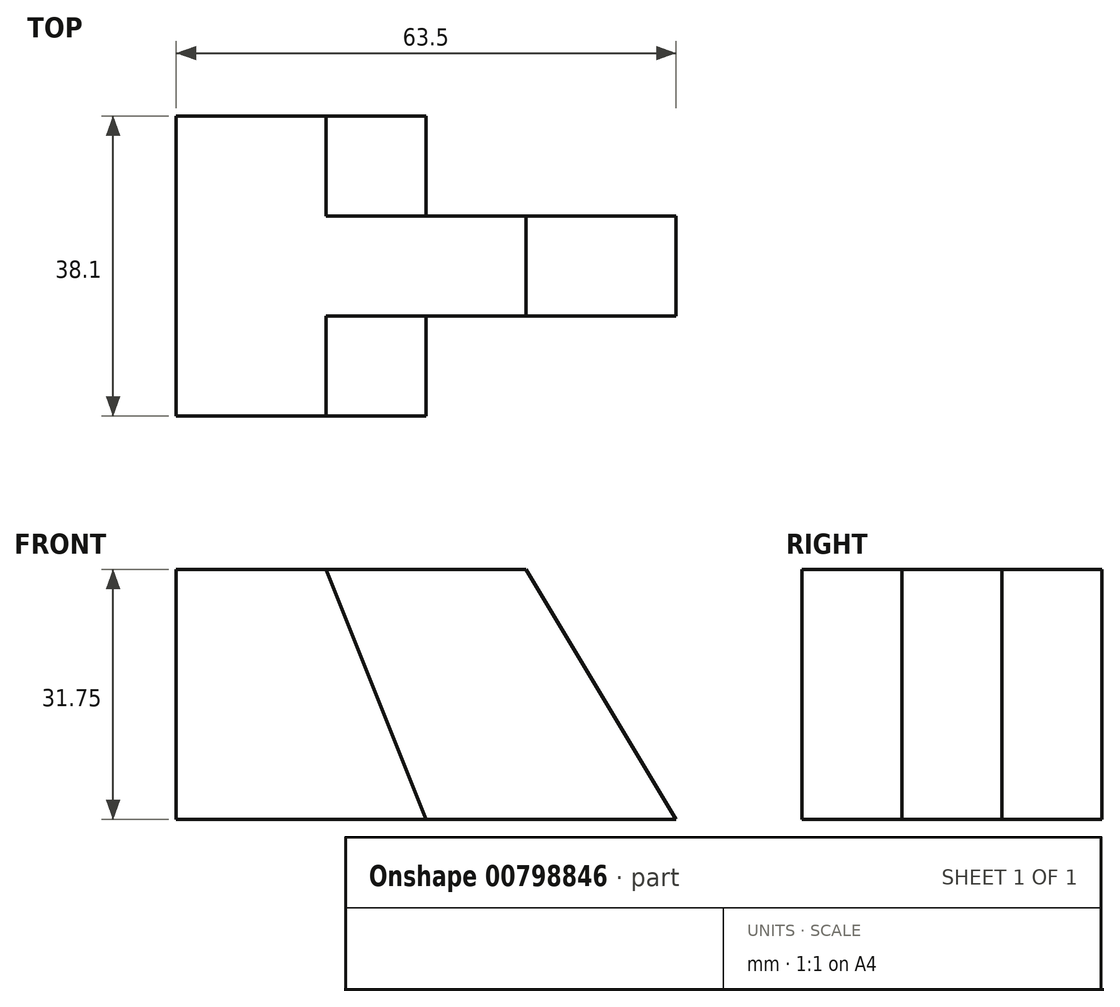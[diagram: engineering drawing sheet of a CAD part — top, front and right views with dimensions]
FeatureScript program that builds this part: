
annotation { "Feature Type Name" : "Feature", "Feature Type Description" : "" }
export const myFeature = defineFeature(function(context is Context, id is Id, definition is map)
    precondition{}
    {
        {
            var Q0;
            Q0=qCreatedBy(makeId("Top.planeOp"),FACE);
            var sketch = newSketch(context, id + "F0", { "sketchPlane" : qUnion([Q0])});
            skLineSegment(sketch, "E0", {"start": v(0, 0) * mm, "end": v(31.75, 0) * mm});
            skLineSegment(sketch, "E1", {"start": v(31.75, 0) * mm, "end": v(31.75, 12.7) * mm});
            skLineSegment(sketch, "E2", {"start": v(31.75, 12.7) * mm, "end": v(63.5, 12.7) * mm});
            skLineSegment(sketch, "E3", {"start": v(0, 0) * mm, "end": v(0, 38.1) * mm});
            skLineSegment(sketch, "E4", {"start": v(0, 38.1) * mm, "end": v(31.75, 38.1) * mm});
            skLineSegment(sketch, "E5", {"start": v(31.75, 38.1) * mm, "end": v(31.75, 25.4) * mm});
            skLineSegment(sketch, "E6", {"start": v(31.75, 25.4) * mm, "end": v(63.5, 25.4) * mm});
            skLineSegment(sketch, "E7", {"start": v(63.5, 25.4) * mm, "end": v(63.5, 12.7) * mm});
            skSolve(sketch);
        }
        {
            var Q0;
            Q0 = qSketchRegion(id + "F0", true);
            extrude(context, id + "F1", {"entities" : qUnion([Q0]), "depth" : 31.75 * mm, "offsetDistance" : 25.4 * mm});
        }
        {
            var Q0;
            Q0=makeQuery(id+"F1.opExtrude","SWEPT_FACE",FACE,{"disambiguationData":[OSD([sQuery(id+"F0.wireOp",EDGE,"E0")])]});
            var sketch = newSketch(context, id + "F2", { "sketchPlane" : qUnion([Q0])});
            skLineSegment(sketch, "E8", {"start": v(0, 31.75) * mm, "end": v(19.05, 31.75) * mm});
            skLineSegment(sketch, "E9", {"start": v(19.05, 31.75) * mm, "end": v(31.75, 0) * mm});
            skSolve(sketch);
        }
        {
            var Q0;
            {var subQ0=sQuery(id+"F2.wireOp",EDGE,"E9");Q0=makeQuery(id+"F2.imprint","IMPRINT",FACE,{"disambiguationData":[TD([[makeQuery(id+"F2.imprint","IMPRINT",EDGE,{"derivedFrom":subQ0}),1.0]])]});}
            extrude(context, id + "F3", {"entities" : qUnion([Q0]), "operationType" : NewBodyOperationType.REMOVE, "oppositeDirection" : true, "depth" : 12.7 * mm, "offsetDistance" : 25.4 * mm});
        }
        {
            var Q0;
            Q0=makeQuery(id+"F3.boolean.opBoolean","MERGE",FACE,{"derivedFrom":[makeQuery(id+"F1.opExtrude","SWEPT_FACE",FACE,{"disambiguationData":[OSD([sQuery(id+"F0.wireOp",EDGE,"E2")])]}),makeQuery(id+"F3.opExtrude","CAP_FACE",FACE,{"disambiguationData":[OSD([sQuery(id+"F0.wireOp",EDGE,"E0"),sQuery(id+"F0.wireOp",EDGE,"E1"),sQuery(id+"F2.wireOp",EDGE,"E9")])],"isStart":false})]});
            var sketch = newSketch(context, id + "F4", { "sketchPlane" : qUnion([Q0])});
            skLineSegment(sketch, "E10", {"start": v(19.05, 31.75) * mm, "end": v(44.45, 31.75) * mm});
            skLineSegment(sketch, "E11", {"start": v(44.45, 31.75) * mm, "end": v(63.5, 0) * mm});
            skSolve(sketch);
        }
        {
            var Q0;
            {var subQ0=sQuery(id+"F4.wireOp",EDGE,"E11");Q0=makeQuery(id+"F4.imprint","IMPRINT",FACE,{"disambiguationData":[TD([[makeQuery(id+"F4.imprint","IMPRINT",EDGE,{"derivedFrom":subQ0}),1.0]])]});}
            extrude(context, id + "F5", {"entities" : qUnion([Q0]), "operationType" : NewBodyOperationType.REMOVE, "endBound" : BoundingType.THROUGH_ALL, "oppositeDirection" : true, "depth" : 25.4 * mm, "offsetDistance" : 25.4 * mm});
        }
        {
            var Q0;
            Q0=makeQuery(id+"F1.opExtrude","SWEPT_FACE",FACE,{"disambiguationData":[OSD([sQuery(id+"F0.wireOp",EDGE,"E4")])]});
            var sketch = newSketch(context, id + "F6", { "sketchPlane" : qUnion([Q0])});
            skLineSegment(sketch, "E12", {"start": v(0, 31.75) * mm, "end": v(-19.05, 31.75) * mm});
            skLineSegment(sketch, "E13", {"start": v(-19.05, 31.75) * mm, "end": v(-31.75, 0) * mm});
            skSolve(sketch);
        }
        {
            var Q0;
            {var subQ0=sQuery(id+"F6.wireOp",EDGE,"E13");Q0=makeQuery(id+"F6.imprint","IMPRINT",FACE,{"disambiguationData":[TD([[makeQuery(id+"F6.imprint","IMPRINT",EDGE,{"derivedFrom":subQ0}),-1.0]])]});}
            extrude(context, id + "F7", {"entities" : qUnion([Q0]), "operationType" : NewBodyOperationType.REMOVE, "oppositeDirection" : true, "depth" : 12.7 * mm, "offsetDistance" : 25.4 * mm});
        }
    });
